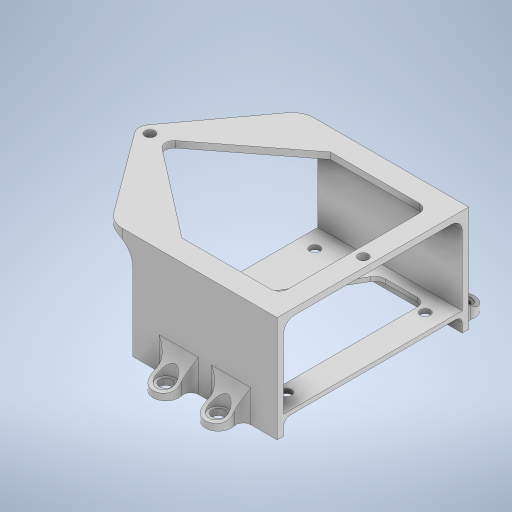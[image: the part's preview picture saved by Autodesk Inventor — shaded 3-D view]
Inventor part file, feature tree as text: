
AUTODESK INVENTOR PART (.ipt)
format: ipt  version: 2024 (Build 280153000, 153)  size: 532,480 bytes
history: native  units: in
note: dims shown in document units (in); Inventor stores cm internally (conversion verified against a paired STEP export)
features: extrude x8, fillet x7, projected_geometry x2, plane x1
ambient origin geometry x8: Origin, YZ Plane, XZ Plane, XY Plane, X Axis, Y Axis, Z Axis, Center Point
bodies: Solid1 (feature_tree)
feature tree (18):
  extrude  "Extrusion1"  Depth=3.2874in
  extrude  "Extrusion2"  Depth=0.1181in
  extrude  "Extrusion3"  Depth=0.1181in
  extrude  "Extrusion5"  Depth=0.1969in
  extrude  "Extrusion6"  Depth=0.1969in
  fillet  "Fillet1"  Radius=0.4724in
  extrude  "Extrusion7"  Depth=0.4724in
  extrude  "Extrusion8"  Depth=2.6575in
  plane  "Work Plane1"
  extrude  "Extrusion9"  Depth=1.3287in
  fillet  "Fillet2"  Radius=1.6437in
  fillet  "Fillet3"  Radius=0.0787in
  fillet  "Fillet4"  Radius=1.5551in
  fillet  "Fillet5"  Radius=0.2756in
  fillet  "Fillet6"  Radius=0.2756in
  fillet  "Fillet7"  Radius=4.3504in
  projected_geometry  "Projected Loop1"
  projected_geometry  "Projected Loop2"
